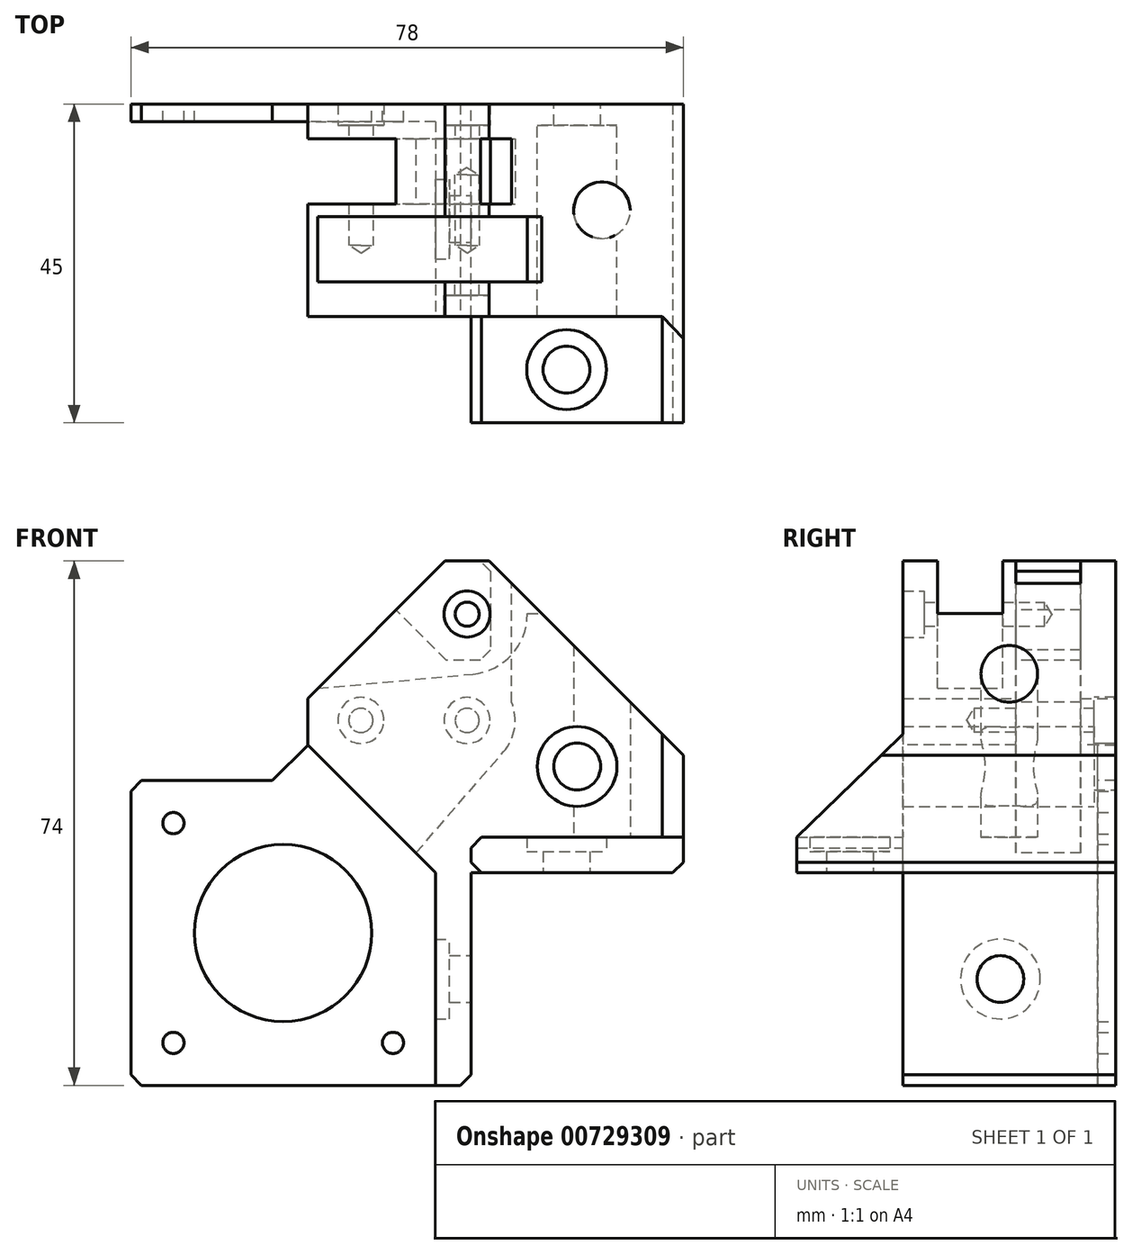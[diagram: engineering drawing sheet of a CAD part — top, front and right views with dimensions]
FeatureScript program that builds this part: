
annotation { "Feature Type Name" : "Feature", "Feature Type Description" : "" }
export const myFeature = defineFeature(function(context is Context, id is Id, definition is map)
    precondition{}
    {
        {
            var Q0;
            Q0=qCreatedBy(makeId("Front.planeOp"),FACE);
            cPlane(context, id + "F0", {"entities" : qUnion([Q0]), "cplaneType" : CPlaneType.OFFSET, "offset" : 15 * mm, "width" : 150 * mm, "height" : 150 * mm});
        }
        {
            var Q0;
            Q0=qCreatedBy(id+"F0.planeOp",FACE);
            cPlane(context, id + "F1", {"entities" : qUnion([Q0]), "cplaneType" : CPlaneType.OFFSET, "offset" : 0.9 * mm, "width" : 150 * mm, "height" : 150 * mm});
        }
        {
            var Q0;
            Q0=qCreatedBy(id+"F0.planeOp",FACE);
            cPlane(context, id + "F2", {"entities" : qUnion([Q0]), "cplaneType" : CPlaneType.OFFSET, "offset" : 0.9 * mm, "oppositeDirection" : true, "width" : 150 * mm, "height" : 150 * mm});
        }
        {
            var Q0;
            Q0=qCreatedBy(makeId("Front.planeOp"),FACE);
            var sketch = newSketch(context, id + "F3", { "sketchPlane" : qUnion([Q0])});
            skLineSegment(sketch, "E0.bottom", {"start": v(0, 0) * mm, "end": v(5, 0) * mm, "construction": true});
            skLineSegment(sketch, "E0.top", {"start": v(0, 30) * mm, "end": v(5, 30) * mm, "construction": true});
            skLineSegment(sketch, "E0.left", {"start": v(0, 0) * mm, "end": v(0, 30) * mm, "construction": true});
            skLineSegment(sketch, "E0.right", {"start": v(5, 0) * mm, "end": v(5, 30) * mm, "construction": true});
            skLineSegment(sketch, "E1.bottom", {"start": v(5, 30) * mm, "end": v(35, 30) * mm, "construction": true});
            skLineSegment(sketch, "E1.top", {"start": v(5, 0) * mm, "end": v(35, 0) * mm, "construction": true});
            skLineSegment(sketch, "E1.left", {"start": v(5, 30) * mm, "end": v(5, 0) * mm, "construction": true});
            skLineSegment(sketch, "E1.right", {"start": v(35, 30) * mm, "end": v(35, 0) * mm, "construction": true});
            skLineSegment(sketch, "E2", {"start": v(12, 30) * mm, "end": v(12, 0) * mm, "construction": true});
            skLineSegment(sketch, "E3", {"start": v(12, 0) * mm, "end": v(12, 15) * mm, "construction": true});
            skLineSegment(sketch, "E4", {"start": v(12, 15) * mm, "end": v(35, 15) * mm, "construction": true});
            skPoint(sketch, "E5", {"position": v(23.5, 15) * mm});
            skLineSegment(sketch, "E6.bottom", {"start": v(0, 0) * mm, "end": v(-43, 0) * mm, "construction": true});
            skLineSegment(sketch, "E6.top", {"start": v(0, 43) * mm, "end": v(-43, 43) * mm, "construction": true});
            skLineSegment(sketch, "E6.left", {"start": v(0, 0) * mm, "end": v(0, 43) * mm, "construction": true});
            skLineSegment(sketch, "E6.right", {"start": v(-43, 0) * mm, "end": v(-43, 43) * mm, "construction": true});
            skPoint(sketch, "E6.middle", {"position": v(-21.5, 21.5) * mm});
            skLineSegment(sketch, "E7.bottom", {"start": v(-6, 6) * mm, "end": v(-37, 6) * mm, "construction": true});
            skLineSegment(sketch, "E7.top", {"start": v(-6, 37) * mm, "end": v(-37, 37) * mm, "construction": true});
            skLineSegment(sketch, "E7.left", {"start": v(-6, 6) * mm, "end": v(-6, 37) * mm, "construction": true});
            skLineSegment(sketch, "E7.right", {"start": v(-37, 6) * mm, "end": v(-37, 37) * mm, "construction": true});
            skLineSegment(sketch, "E8", {"start": v(35, 75) * mm, "end": v(0, 75) * mm, "construction": true});
            skCircle(sketch, "E9", {"center": v(-10.53, 51.5) * mm, "radius": 1.5 * mm, "construction": true});
            skCircle(sketch, "E10", {"center": v(-10.53, 51.5) * mm, "radius": 6.5 * mm, "construction": true});
            skCircle(sketch, "E11", {"center": v(4.47, 51.5) * mm, "radius": 6.5 * mm, "construction": true});
            skCircle(sketch, "E12", {"center": v(4.47, 51.5) * mm, "radius": 1.5 * mm, "construction": true});
            skCircle(sketch, "E13", {"center": v(4.47, 66.5) * mm, "radius": 6.5 * mm, "construction": true});
            skCircle(sketch, "E14", {"center": v(4.47, 66.5) * mm, "radius": 1.5 * mm, "construction": true});
            skCircle(sketch, "E15", {"center": v(4.47, 51.5) * mm, "radius": 4.78 * mm, "construction": true});
            skLineSegment(sketch, "E16", {"start": v(4.47, 51.5) * mm, "end": v(9.25, 51.5) * mm, "construction": true});
            skSolve(sketch);
        }
        {
            var Q0;
            Q0=qCreatedBy(makeId("Front.planeOp"),FACE);
            var sketch = newSketch(context, id + "F4", { "sketchPlane" : qUnion([Q0])});
            skLineSegment(sketch, "E17", {"start": v(7.58, 74) * mm, "end": v(35, 46.58) * mm});
            skLineSegment(sketch, "E18", {"start": v(35, 46.58) * mm, "end": v(35, 30) * mm});
            skLineSegment(sketch, "E19", {"start": v(35, 30) * mm, "end": v(5, 30) * mm});
            skLineSegment(sketch, "E20", {"start": v(5, 30) * mm, "end": v(5, 0) * mm});
            skLineSegment(sketch, "E21", {"start": v(5, 0) * mm, "end": v(-43, 0) * mm});
            skLineSegment(sketch, "E22", {"start": v(7.58, 74) * mm, "end": v(1.36, 74) * mm});
            skLineSegment(sketch, "E23", {"start": v(1.36, 74) * mm, "end": v(-18.03, 54.6) * mm});
            skLineSegment(sketch, "E24", {"start": v(-18.03, 43) * mm, "end": v(-43, 43) * mm});
            skLineSegment(sketch, "E25", {"start": v(-43, 43) * mm, "end": v(-43, 0) * mm});
            skLineSegment(sketch, "E26", {"start": v(-18.03, 54.6) * mm, "end": v(-18.03, 43) * mm});
            skSolve(sketch);
        }
        {
            var Q0;
            Q0 = qSketchRegion(id + "F4", true);
            extrude(context, id + "F5", {"entities" : qUnion([Q0]), "depth" : 30 * mm, "offsetDistance" : 25 * mm});
        }
        {
            var Q0;
            Q0=makeQuery(id+"F5.opExtrude","CAP_FACE",FACE,{"disambiguationData":[OSD([sQuery(id+"F4.wireOp",EDGE,"E17"),sQuery(id+"F4.wireOp",EDGE,"E18"),sQuery(id+"F4.wireOp",EDGE,"E19"),sQuery(id+"F4.wireOp",EDGE,"E20"),sQuery(id+"F4.wireOp",EDGE,"E21"),sQuery(id+"F4.wireOp",EDGE,"E22"),sQuery(id+"F4.wireOp",EDGE,"E23"),sQuery(id+"F4.wireOp",EDGE,"E24"),sQuery(id+"F4.wireOp",EDGE,"E25"),sQuery(id+"F4.wireOp",EDGE,"E26")])],"isStart":false});
            var sketch = newSketch(context, id + "F6", { "sketchPlane" : qUnion([Q0])});
            skLineSegment(sketch, "E27", {"start": v(-43, 0) * mm, "end": v(0, 0) * mm});
            skLineSegment(sketch, "E28", {"start": v(0, 0) * mm, "end": v(0, 30) * mm});
            skLineSegment(sketch, "E29", {"start": v(0, 30) * mm, "end": v(-18.03, 48.03) * mm});
            skLineSegment(sketch, "E30", {"start": v(-18.03, 48.03) * mm, "end": v(-18.03, 43) * mm});
            skLineSegment(sketch, "E31", {"start": v(-18.03, 43) * mm, "end": v(-43, 43) * mm});
            skLineSegment(sketch, "E32", {"start": v(-43, 43) * mm, "end": v(-43, 0) * mm});
            skSolve(sketch);
        }
        {
            var Q0;
            Q0=makeQuery(id+"F6.imprint","IMPRINT",FACE,{"disambiguationData":[TD([[makeQuery(id+"F6.imprint","IMPRINT",EDGE,{"derivedFrom":sQuery(id+"F6.wireOp",EDGE,"E27")}),-1.0]])]});
            extrude(context, id + "F7", {"entities" : qUnion([Q0]), "operationType" : NewBodyOperationType.REMOVE, "oppositeDirection" : true, "depth" : 27.5 * mm, "offsetDistance" : 25 * mm});
        }
        {
            var Q0;
            Q0=qCreatedBy(id+"F2.planeOp",FACE);
            var sketch = newSketch(context, id + "F8", { "sketchPlane" : qUnion([Q0])});
            skLineSegment(sketch, "E33", {"start": v(-2.77, 32.77) * mm, "end": v(9.6, 47.06) * mm});
            skCircle(sketch, "E34", {"center": v(-21.5, 21.5) * mm, "radius": 4.78 * mm, "construction": true});
            skLineSegment(sketch, "E35", {"start": v(-17.89, 18.37) * mm, "end": v(8.08, 48.37) * mm, "construction": true});
            skArc(sketch, "E36", {"start": v(9.6, 47.06) * mm, "mid": v(11.16, 50.4) * mm, "end": v(10.75, 54.06) * mm});
            skLineSegment(sketch, "E37", {"start": v(10.75, 54.06) * mm, "end": v(10.75, 70.83) * mm});
            skLineSegment(sketch, "E38", {"start": v(10.75, 70.83) * mm, "end": v(7.58, 74) * mm});
            skLineSegment(sketch, "E39", {"start": v(7.75, 72.59) * mm, "end": v(7.75, 61.41) * mm});
            skLineSegment(sketch, "E40", {"start": v(-5.57, 67.07) * mm, "end": v(-18.03, 54.6) * mm});
            skLineSegment(sketch, "E41", {"start": v(-18.03, 54.6) * mm, "end": v(-18.03, 48.03) * mm});
            skLineSegment(sketch, "E42", {"start": v(-18.03, 48.03) * mm, "end": v(-2.77, 32.77) * mm});
            skLineSegment(sketch, "E43", {"start": v(7.75, 61.41) * mm, "end": v(6.34, 60) * mm});
            skLineSegment(sketch, "E44", {"start": v(6.34, 60) * mm, "end": v(1.5, 60) * mm});
            skLineSegment(sketch, "E45", {"start": v(1.5, 60) * mm, "end": v(-5.57, 67.07) * mm});
            skLineSegment(sketch, "E46", {"start": v(10.75, 62.44) * mm, "end": v(7.75, 62.44) * mm, "construction": true});
            skPoint(sketch, "E47", {"position": v(9.25, 62.44) * mm});
            skLineSegment(sketch, "E48", {"start": v(7.75, 72.59) * mm, "end": v(6.34, 74) * mm});
            skLineSegment(sketch, "E49", {"start": v(6.34, 74) * mm, "end": v(7.58, 74) * mm});
            skSolve(sketch);
        }
        {
            var Q0;
            Q0 = qSketchRegion(id + "F8", true);
            extrude(context, id + "F9", {"entities" : qUnion([Q0]), "operationType" : NewBodyOperationType.REMOVE, "oppositeDirection" : true, "depth" : 9.2 * mm, "offsetDistance" : 25 * mm});
        }
        {
            var Q0;
            Q0=qCreatedBy(id+"F1.planeOp",FACE);
            var sketch = newSketch(context, id + "F10", { "sketchPlane" : qUnion([Q0])});
            skLineSegment(sketch, "E50", {"start": v(-16.62, 56.02) * mm, "end": v(5.25, 58.04) * mm});
            skLineSegment(sketch, "E51", {"start": v(-16.62, 56.02) * mm, "end": v(1.36, 74) * mm});
            skLineSegment(sketch, "E52", {"start": v(1.36, 74) * mm, "end": v(7.58, 74) * mm});
            skArc(sketch, "E53", {"start": v(5.25, 58.04) * mm, "mid": v(10.75, 60.77) * mm, "end": v(12.97, 66.5) * mm});
            skLineSegment(sketch, "E54", {"start": v(12.97, 66.5) * mm, "end": v(12.97, 66.6) * mm});
            skLineSegment(sketch, "E55", {"start": v(12.97, 66.6) * mm, "end": v(14.97, 66.6) * mm});
            skLineSegment(sketch, "E56", {"start": v(14.97, 66.6) * mm, "end": v(7.58, 74) * mm});
            skSolve(sketch);
        }
        {
            var Q0;
            Q0 = qSketchRegion(id + "F10", true);
            extrude(context, id + "F11", {"entities" : qUnion([Q0]), "operationType" : NewBodyOperationType.REMOVE, "depth" : 9.2 * mm, "offsetDistance" : 25 * mm});
        }
        {
            var Q0;
            Q0=makeQuery(id+"F5.opExtrude","CAP_FACE",FACE,{"disambiguationData":[OSD([sQuery(id+"F4.wireOp",EDGE,"E17"),sQuery(id+"F4.wireOp",EDGE,"E18"),sQuery(id+"F4.wireOp",EDGE,"E19"),sQuery(id+"F4.wireOp",EDGE,"E20"),sQuery(id+"F4.wireOp",EDGE,"E21"),sQuery(id+"F4.wireOp",EDGE,"E22"),sQuery(id+"F4.wireOp",EDGE,"E23"),sQuery(id+"F4.wireOp",EDGE,"E24"),sQuery(id+"F4.wireOp",EDGE,"E25"),sQuery(id+"F4.wireOp",EDGE,"E26")])],"isStart":false});
            var sketch = newSketch(context, id + "F12", { "sketchPlane" : qUnion([Q0])});
            skPoint(sketch, "E57", {"position": v(20, 45) * mm});
            skPoint(sketch, "E57.positionSnap0", {"position": v(20, 30) * mm});
            skSolve(sketch);
        }
        {
            var Q0;
            Q0=sQuery(id+"F12.wireOp",VERTEX,"E57");
            var Q1;
            Q1=makeQuery(id+"F5.opExtrude","SWEPT_BODY",BODY,{"disambiguationData":[OSD([sQuery(id+"F4.wireOp",EDGE,"E17"),sQuery(id+"F4.wireOp",EDGE,"E18"),sQuery(id+"F4.wireOp",EDGE,"E19"),sQuery(id+"F4.wireOp",EDGE,"E20"),sQuery(id+"F4.wireOp",EDGE,"E21"),sQuery(id+"F4.wireOp",EDGE,"E22"),sQuery(id+"F4.wireOp",EDGE,"E23"),sQuery(id+"F4.wireOp",EDGE,"E24"),sQuery(id+"F4.wireOp",EDGE,"E25"),sQuery(id+"F4.wireOp",EDGE,"E26")])]});
            hole(context, id + "F13", {"style" : HoleStyle.C_BORE, "endStyle" : HoleEndStyle.THROUGH, "holeDiameter" : 6.6 * mm, "cBoreDiameter" : 11.25 * mm, "cBoreDepth" : 27 * mm, "majorDiameter" : 5 * mm, "isTappedThrough" : true, "tappedDepth" : 12 * mm, "tapClearance" : 3, "locations" : qUnion([Q0]), "scope" : qUnion([Q1])});
        }
        {
            var Q0;
            Q0=makeQuery(id+"F5.opExtrude","SWEPT_FACE",FACE,{"disambiguationData":[OSD([sQuery(id+"F4.wireOp",EDGE,"E19")])]});
            cPlane(context, id + "F14", {"entities" : qUnion([Q0]), "cplaneType" : CPlaneType.OFFSET, "offset" : 5 * mm, "oppositeDirection" : true, "width" : 150 * mm, "height" : 150 * mm});
        }
        {
            var Q0;
            Q0=qCreatedBy(id+"F14.planeOp",FACE);
            var sketch = newSketch(context, id + "F15", { "sketchPlane" : qUnion([Q0])});
            skCircle(sketch, "E58", {"center": v(23.5, 15) * mm, "radius": 4 * mm});
            skSolve(sketch);
        }
        {
            var Q0;
            Q0 = qSketchRegion(id + "F15", true);
            extrude(context, id + "F16", {"entities" : qUnion([Q0]), "operationType" : NewBodyOperationType.REMOVE, "endBound" : BoundingType.THROUGH_ALL, "oppositeDirection" : true, "depth" : 25 * mm, "offsetDistance" : 25 * mm});
        }
        {
            var Q0;
            Q0=makeQuery(id+"F7.boolean.opBoolean","COPY",FACE,{"derivedFrom":makeQuery(id+"F7.opExtrude","SWEPT_FACE",FACE,{"disambiguationData":[OSD([sQuery(id+"F6.wireOp",EDGE,"E28")])]})});
            var sketch = newSketch(context, id + "F17", { "sketchPlane" : qUnion([Q0])});
            skPoint(sketch, "E59", {"position": v(16.25, 15) * mm});
            skPoint(sketch, "E59.positionSnap0", {"position": v(16.25, 0) * mm});
            skSolve(sketch);
        }
        {
            var Q0;
            Q0=sQuery(id+"F17.wireOp",VERTEX,"E59");
            var Q1;
            Q1=makeQuery(id+"F5.opExtrude","SWEPT_BODY",BODY,{"disambiguationData":[OSD([sQuery(id+"F4.wireOp",EDGE,"E17"),sQuery(id+"F4.wireOp",EDGE,"E18"),sQuery(id+"F4.wireOp",EDGE,"E19"),sQuery(id+"F4.wireOp",EDGE,"E20"),sQuery(id+"F4.wireOp",EDGE,"E21"),sQuery(id+"F4.wireOp",EDGE,"E22"),sQuery(id+"F4.wireOp",EDGE,"E23"),sQuery(id+"F4.wireOp",EDGE,"E24"),sQuery(id+"F4.wireOp",EDGE,"E25"),sQuery(id+"F4.wireOp",EDGE,"E26")])]});
            hole(context, id + "F18", {"style" : HoleStyle.C_BORE, "endStyle" : HoleEndStyle.THROUGH, "holeDiameter" : 6.6 * mm, "cBoreDiameter" : 11.25 * mm, "cBoreDepth" : 2 * mm, "majorDiameter" : 5 * mm, "isTappedThrough" : true, "tappedDepth" : 12 * mm, "tapClearance" : 3, "locations" : qUnion([Q0]), "scope" : qUnion([Q1])});
        }
        {
            var Q0;
            Q0=makeQuery(id+"F5.opExtrude","CAP_FACE",FACE,{"disambiguationData":[OSD([sQuery(id+"F4.wireOp",EDGE,"E17"),sQuery(id+"F4.wireOp",EDGE,"E18"),sQuery(id+"F4.wireOp",EDGE,"E19"),sQuery(id+"F4.wireOp",EDGE,"E20"),sQuery(id+"F4.wireOp",EDGE,"E21"),sQuery(id+"F4.wireOp",EDGE,"E22"),sQuery(id+"F4.wireOp",EDGE,"E23"),sQuery(id+"F4.wireOp",EDGE,"E24"),sQuery(id+"F4.wireOp",EDGE,"E25"),sQuery(id+"F4.wireOp",EDGE,"E26")])],"isStart":false});
            var sketch = newSketch(context, id + "F19", { "sketchPlane" : qUnion([Q0])});
            skLineSegment(sketch, "E60.bottom", {"start": v(35, 30) * mm, "end": v(5, 30) * mm});
            skLineSegment(sketch, "E60.top", {"start": v(32, 35) * mm, "end": v(5, 35) * mm});
            skLineSegment(sketch, "E60.left", {"start": v(35, 30) * mm, "end": v(35, 35) * mm});
            skLineSegment(sketch, "E60.right", {"start": v(5, 30) * mm, "end": v(5, 35) * mm});
            skLineSegment(sketch, "E61", {"start": v(35, 35) * mm, "end": v(35, 46.58) * mm});
            skLineSegment(sketch, "E62", {"start": v(35, 46.58) * mm, "end": v(32, 49.58) * mm});
            skLineSegment(sketch, "E63", {"start": v(32, 49.58) * mm, "end": v(32, 35) * mm});
            skSolve(sketch);
        }
        {
            var Q0;
            Q0=makeQuery(id+"F19.imprint","IMPRINT",FACE,{"disambiguationData":[TD([[makeQuery(id+"F19.imprint","IMPRINT",EDGE,{"derivedFrom":sQuery(id+"F19.wireOp",EDGE,"E60.bottom")}),-1.0]])]});
            extrude(context, id + "F20", {"entities" : qUnion([Q0]), "operationType" : NewBodyOperationType.ADD, "depth" : 15 * mm, "offsetDistance" : 25 * mm});
        }
        {
            var Q0;
            Q0=makeQuery(id+"F20.opExtrude","SWEPT_FACE",FACE,{"disambiguationData":[OSD([sQuery(id+"F19.wireOp",EDGE,"E60.top")])]});
            var sketch = newSketch(context, id + "F21", { "sketchPlane" : qUnion([Q0])});
            skPoint(sketch, "E64", {"position": v(18.5, -37.5) * mm});
            skPoint(sketch, "E64.positionSnap0", {"position": v(18.5, -45) * mm});
            skPoint(sketch, "E64.positionSnap1", {"position": v(5, -37.5) * mm});
            skSolve(sketch);
        }
        {
            var Q0;
            Q0=sQuery(id+"F21.wireOp",VERTEX,"E64");
            var Q1;
            Q1=makeQuery(id+"F5.opExtrude","SWEPT_BODY",BODY,{"disambiguationData":[OSD([sQuery(id+"F4.wireOp",EDGE,"E17"),sQuery(id+"F4.wireOp",EDGE,"E18"),sQuery(id+"F4.wireOp",EDGE,"E19"),sQuery(id+"F4.wireOp",EDGE,"E20"),sQuery(id+"F4.wireOp",EDGE,"E21"),sQuery(id+"F4.wireOp",EDGE,"E22"),sQuery(id+"F4.wireOp",EDGE,"E23"),sQuery(id+"F4.wireOp",EDGE,"E24"),sQuery(id+"F4.wireOp",EDGE,"E25"),sQuery(id+"F4.wireOp",EDGE,"E26")])]});
            hole(context, id + "F22", {"style" : HoleStyle.C_BORE, "endStyle" : HoleEndStyle.THROUGH, "holeDiameter" : 6.6 * mm, "cBoreDiameter" : 11.25 * mm, "cBoreDepth" : 2 * mm, "majorDiameter" : 5 * mm, "isTappedThrough" : true, "tappedDepth" : 12 * mm, "tapClearance" : 3, "locations" : qUnion([Q0]), "scope" : qUnion([Q1])});
        }
        {
            var Q0;
            Q0=makeQuery(id+"F20.opExtrude","SWEPT_FACE",FACE,{"disambiguationData":[OSD([sQuery(id+"F19.wireOp",EDGE,"E63")])]});
            var sketch = newSketch(context, id + "F23", { "sketchPlane" : qUnion([Q0])});
            skLineSegment(sketch, "E65", {"start": v(30, 49.58) * mm, "end": v(45, 35) * mm});
            skLineSegment(sketch, "E66", {"start": v(45, 35) * mm, "end": v(45, 49.58) * mm});
            skLineSegment(sketch, "E67", {"start": v(45, 49.58) * mm, "end": v(30, 49.58) * mm});
            skSolve(sketch);
        }
        {
            var Q0;
            Q0=makeQuery(id+"F23.imprint","IMPRINT",FACE,{"disambiguationData":[TD([[makeQuery(id+"F23.imprint","IMPRINT",EDGE,{"derivedFrom":sQuery(id+"F23.wireOp",EDGE,"E65")}),1.0]])]});
            extrude(context, id + "F24", {"entities" : qUnion([Q0]), "operationType" : NewBodyOperationType.REMOVE, "endBound" : BoundingType.THROUGH_ALL, "oppositeDirection" : true, "depth" : 25 * mm, "offsetDistance" : 25 * mm});
        }
        {
            var Q0;
            Q0=makeQuery(id+"F5.opExtrude","CAP_FACE",FACE,{"disambiguationData":[OSD([sQuery(id+"F4.wireOp",EDGE,"E17"),sQuery(id+"F4.wireOp",EDGE,"E18"),sQuery(id+"F4.wireOp",EDGE,"E19"),sQuery(id+"F4.wireOp",EDGE,"E20"),sQuery(id+"F4.wireOp",EDGE,"E21"),sQuery(id+"F4.wireOp",EDGE,"E22"),sQuery(id+"F4.wireOp",EDGE,"E23"),sQuery(id+"F4.wireOp",EDGE,"E24"),sQuery(id+"F4.wireOp",EDGE,"E25"),sQuery(id+"F4.wireOp",EDGE,"E26")])],"isStart":true});
            var sketch = newSketch(context, id + "F25", { "sketchPlane" : qUnion([Q0])});
            skCircle(sketch, "E68", {"center": v(37, 37) * mm, "radius": 1.5 * mm});
            skCircle(sketch, "E69", {"center": v(37, 6) * mm, "radius": 1.5 * mm});
            skCircle(sketch, "E70", {"center": v(6, 6) * mm, "radius": 1.5 * mm});
            skCircle(sketch, "E71", {"center": v(21.5, 21.5) * mm, "radius": 12.5 * mm});
            skSolve(sketch);
        }
        {
            var Q0;
            Q0 = qSketchRegion(id + "F25", true);
            extrude(context, id + "F26", {"entities" : qUnion([Q0]), "operationType" : NewBodyOperationType.REMOVE, "endBound" : BoundingType.THROUGH_ALL, "oppositeDirection" : true, "depth" : 25 * mm, "offsetDistance" : 25 * mm});
        }
        {
            var Q0;
            Q0=makeQuery(id+"F5.opExtrude","CAP_FACE",FACE,{"disambiguationData":[OSD([sQuery(id+"F4.wireOp",EDGE,"E17"),sQuery(id+"F4.wireOp",EDGE,"E18"),sQuery(id+"F4.wireOp",EDGE,"E19"),sQuery(id+"F4.wireOp",EDGE,"E20"),sQuery(id+"F4.wireOp",EDGE,"E21"),sQuery(id+"F4.wireOp",EDGE,"E22"),sQuery(id+"F4.wireOp",EDGE,"E23"),sQuery(id+"F4.wireOp",EDGE,"E24"),sQuery(id+"F4.wireOp",EDGE,"E25"),sQuery(id+"F4.wireOp",EDGE,"E26")])],"isStart":false});
            var sketch = newSketch(context, id + "F27", { "sketchPlane" : qUnion([Q0])});
            skPoint(sketch, "E72.0", {"position": v(4.47, 66.5) * mm});
            skSolve(sketch);
        }
        {
            var Q0;
            Q0=sQuery(id+"F27.wireOp",VERTEX,"E72.0");
            var Q1;
            Q1=makeQuery(id+"F5.opExtrude","SWEPT_BODY",BODY,{"disambiguationData":[OSD([sQuery(id+"F4.wireOp",EDGE,"E17"),sQuery(id+"F4.wireOp",EDGE,"E18"),sQuery(id+"F4.wireOp",EDGE,"E19"),sQuery(id+"F4.wireOp",EDGE,"E20"),sQuery(id+"F4.wireOp",EDGE,"E21"),sQuery(id+"F4.wireOp",EDGE,"E22"),sQuery(id+"F4.wireOp",EDGE,"E23"),sQuery(id+"F4.wireOp",EDGE,"E24"),sQuery(id+"F4.wireOp",EDGE,"E25"),sQuery(id+"F4.wireOp",EDGE,"E26")])]});
            hole(context, id + "F28", {"style" : HoleStyle.C_BORE, "endStyle" : HoleEndStyle.BLIND, "standardTappedOrClearance" : lookupTablePath({ "fit" : "Normal", "standard" : "ISO", "size" : "M3", "type" : "Clearance" }), "standardBlindInLast" : lookupTablePath({ "fit" : "Normal", "standard" : "ISO", "engagement" : "75%", "pitch" : "0.5 mm", "size" : "M3", "type" : "Clearance & tapped" }), "holeDiameter" : 3.4 * mm, "cBoreDiameter" : 6.5 * mm, "cBoreDepth" : 3 * mm, "majorDiameter" : 5 * mm, "holeDepth" : 20 * mm, "isTappedThrough" : true, "tappedDepth" : 12 * mm, "tapClearance" : 3, "locations" : qUnion([Q0]), "scope" : qUnion([Q1])});
        }
        {
            var Q0;
            Q0=makeQuery(id+"F5.opExtrude","CAP_FACE",FACE,{"disambiguationData":[OSD([sQuery(id+"F4.wireOp",EDGE,"E17"),sQuery(id+"F4.wireOp",EDGE,"E18"),sQuery(id+"F4.wireOp",EDGE,"E19"),sQuery(id+"F4.wireOp",EDGE,"E20"),sQuery(id+"F4.wireOp",EDGE,"E21"),sQuery(id+"F4.wireOp",EDGE,"E22"),sQuery(id+"F4.wireOp",EDGE,"E23"),sQuery(id+"F4.wireOp",EDGE,"E24"),sQuery(id+"F4.wireOp",EDGE,"E25"),sQuery(id+"F4.wireOp",EDGE,"E26")])],"isStart":true});
            var sketch = newSketch(context, id + "F29", { "sketchPlane" : qUnion([Q0])});
            skPoint(sketch, "E73.0", {"position": v(-4.47, 51.5) * mm});
            skPoint(sketch, "E74.0", {"position": v(10.53, 51.5) * mm});
            skSolve(sketch);
        }
        {
            var Q0;
            Q0=sQuery(id+"F29.wireOp",VERTEX,"E73.0");
            var Q1;
            Q1=sQuery(id+"F29.wireOp",VERTEX,"E74.0");
            var Q2;
            Q2=makeQuery(id+"F5.opExtrude","SWEPT_BODY",BODY,{"disambiguationData":[OSD([sQuery(id+"F4.wireOp",EDGE,"E17"),sQuery(id+"F4.wireOp",EDGE,"E18"),sQuery(id+"F4.wireOp",EDGE,"E19"),sQuery(id+"F4.wireOp",EDGE,"E20"),sQuery(id+"F4.wireOp",EDGE,"E21"),sQuery(id+"F4.wireOp",EDGE,"E22"),sQuery(id+"F4.wireOp",EDGE,"E23"),sQuery(id+"F4.wireOp",EDGE,"E24"),sQuery(id+"F4.wireOp",EDGE,"E25"),sQuery(id+"F4.wireOp",EDGE,"E26")])]});
            hole(context, id + "F30", {"style" : HoleStyle.C_BORE, "endStyle" : HoleEndStyle.BLIND, "standardTappedOrClearance" : lookupTablePath({ "fit" : "Normal", "standard" : "ISO", "size" : "M3", "type" : "Clearance" }), "standardBlindInLast" : lookupTablePath({ "fit" : "Normal", "standard" : "ISO", "engagement" : "75%", "pitch" : "0.5 mm", "size" : "M3", "type" : "Clearance & tapped" }), "holeDiameter" : 3.4 * mm, "cBoreDiameter" : 6.5 * mm, "cBoreDepth" : 3 * mm, "majorDiameter" : 5 * mm, "holeDepth" : 20 * mm, "isTappedThrough" : true, "tappedDepth" : 12 * mm, "tapClearance" : 3, "locations" : qUnion([Q0, Q1]), "scope" : qUnion([Q2])});
        }
        {
            var Q0;
            Q0=makeQuery(id+"F5.opExtrude","SWEPT_EDGE",EDGE,{"disambiguationData":[OSD([sQuery(id+"F4.wireOp",EDGE,"E24"),sQuery(id+"F4.wireOp",EDGE,"E26")])]});
            chamfer(context, id + "F31", {"entities" : qUnion([Q0]), "width" : 5 * mm, "tangentPropagation" : true});
        }
        {
            var Q0;
            Q0=makeQuery(id+"F5.opExtrude","SWEPT_EDGE",EDGE,{"disambiguationData":[OSD([sQuery(id+"F4.wireOp",EDGE,"E24"),sQuery(id+"F4.wireOp",EDGE,"E25")])]});
            var Q1;
            Q1=makeQuery(id+"F5.opExtrude","SWEPT_EDGE",EDGE,{"disambiguationData":[OSD([sQuery(id+"F4.wireOp",EDGE,"E21"),sQuery(id+"F4.wireOp",EDGE,"E25")])]});
            var Q2;
            Q2=makeQuery(id+"F5.opExtrude","SWEPT_EDGE",EDGE,{"disambiguationData":[OSD([sQuery(id+"F4.wireOp",EDGE,"E20"),sQuery(id+"F4.wireOp",EDGE,"E21")])]});
            var Q3;
            Q3=makeQuery(id+"F20.opExtrude","SWEPT_EDGE",EDGE,{"disambiguationData":[OSD([sQuery(id+"F4.wireOp",EDGE,"E20"),sQuery(id+"F19.wireOp",EDGE,"E60.bottom"),sQuery(id+"F19.wireOp",EDGE,"E60.right")])]});
            var Q4;
            Q4=makeQuery(id+"F20.opExtrude","SWEPT_EDGE",EDGE,{"disambiguationData":[OSD([sQuery(id+"F19.wireOp",EDGE,"E60.top"),sQuery(id+"F19.wireOp",EDGE,"E60.right")])]});
            var Q5;
            Q5=makeQuery(id+"F20.boolean.opBoolean","MERGE",EDGE,{"derivedFrom":[makeQuery(id+"F5.opExtrude","SWEPT_EDGE",EDGE,{"disambiguationData":[OSD([sQuery(id+"F4.wireOp",EDGE,"E18"),sQuery(id+"F4.wireOp",EDGE,"E19")])]}),makeQuery(id+"F20.opExtrude","SWEPT_EDGE",EDGE,{"disambiguationData":[OSD([sQuery(id+"F19.wireOp",EDGE,"E60.bottom"),sQuery(id+"F19.wireOp",EDGE,"E60.left")])]})]});
            chamfer(context, id + "F32", {"entities" : qUnion([Q0, Q1, Q2, Q3, Q4, Q5]), "width" : 1.5 * mm});
        }
    });
